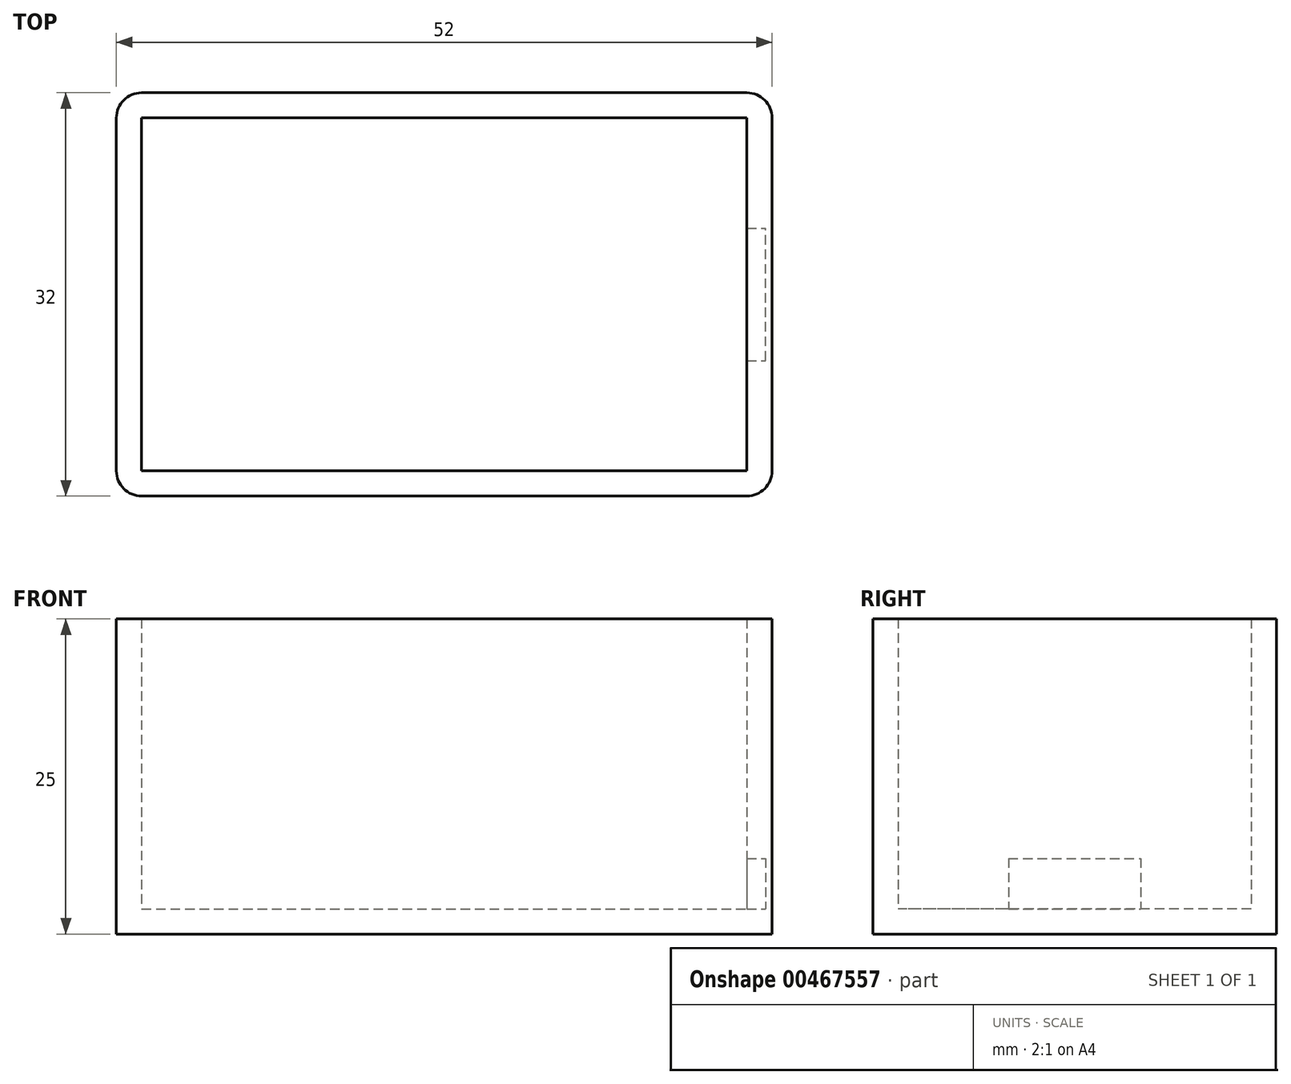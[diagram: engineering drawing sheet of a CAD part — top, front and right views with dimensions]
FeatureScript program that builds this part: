
annotation { "Feature Type Name" : "Feature", "Feature Type Description" : "" }
export const myFeature = defineFeature(function(context is Context, id is Id, definition is map)
    precondition{}
    {
        {
            var Q0;
            Q0=qCreatedBy(makeId("Top.planeOp"),FACE);
            var sketch = newSketch(context, id + "F0", { "sketchPlane" : qUnion([Q0])});
            skLineSegment(sketch, "E0.bottom", {"start": v(-24, 16) * mm, "end": v(24, 16) * mm});
            skLineSegment(sketch, "E0.top", {"start": v(-24, -16) * mm, "end": v(24, -16) * mm});
            skLineSegment(sketch, "E0.left", {"start": v(-26, 14) * mm, "end": v(-26, -14) * mm});
            skLineSegment(sketch, "E0.right", {"start": v(26, 14) * mm, "end": v(26, -14) * mm});
            skPoint(sketch, "E0.middle", {"position": v(0, 0) * mm});
            skPoint(sketch, "E1.visualSharp", {"position": v(-26, 16) * mm});
            skArc(sketch, "E1.filletArc", {"start": v(-24, 16) * mm, "mid": v(-25.41, 15.41) * mm, "end": v(-26, 14) * mm});
            skPoint(sketch, "E2.visualSharp", {"position": v(26, 16) * mm});
            skArc(sketch, "E2.filletArc", {"start": v(26, 14) * mm, "mid": v(25.41, 15.41) * mm, "end": v(24, 16) * mm});
            skPoint(sketch, "E3.visualSharp", {"position": v(-26, -16) * mm});
            skArc(sketch, "E3.filletArc", {"start": v(-26, -14) * mm, "mid": v(-25.41, -15.41) * mm, "end": v(-24, -16) * mm});
            skPoint(sketch, "E4.visualSharp", {"position": v(26, -16) * mm});
            skArc(sketch, "E4.filletArc", {"start": v(24, -16) * mm, "mid": v(25.41, -15.41) * mm, "end": v(26, -14) * mm});
            skSolve(sketch);
        }
        {
            var Q0;
            Q0=makeQuery(id+"F0.imprint","IMPRINT",FACE,{"disambiguationData":[TD([[makeQuery(id+"F0.imprint","IMPRINT",EDGE,{"derivedFrom":sQuery(id+"F0.wireOp",EDGE,"E0.bottom")}),-1.0]])]});
            extrude(context, id + "F1", {"entities" : qUnion([Q0]), "depth" : 25 * mm});
        }
        {
            var Q0;
            Q0=makeQuery(id+"F1.opExtrude","CAP_FACE",FACE,{"disambiguationData":[OSD([sQuery(id+"F0.wireOp",EDGE,"E0.bottom"),sQuery(id+"F0.wireOp",EDGE,"E0.top"),sQuery(id+"F0.wireOp",EDGE,"E0.left"),sQuery(id+"F0.wireOp",EDGE,"E0.right"),sQuery(id+"F0.wireOp",EDGE,"E1.filletArc"),sQuery(id+"F0.wireOp",EDGE,"E2.filletArc"),sQuery(id+"F0.wireOp",EDGE,"E3.filletArc"),sQuery(id+"F0.wireOp",EDGE,"E4.filletArc")])],"isStart":false});
            shell(context, id + "F2", {"entities" : qUnion([Q0]), "thickness" : 2 * mm});
        }
        {
            var Q0;
            Q0=qCreatedBy(makeId("Right.planeOp"),FACE);
            cPlane(context, id + "F3", {"entities" : qUnion([Q0]), "cplaneType" : CPlaneType.OFFSET, "offset" : 25.5 * mm, "width" : 150 * mm, "height" : 150 * mm});
        }
        {
            var Q0;
            Q0=qCreatedBy(id+"F3.planeOp",FACE);
            var sketch = newSketch(context, id + "F4", { "sketchPlane" : qUnion([Q0])});
            skPoint(sketch, "E5", {"position": v(0, 4) * mm});
            skLineSegment(sketch, "E6.bottom", {"start": v(-5.25, 6) * mm, "end": v(5.25, 6) * mm});
            skLineSegment(sketch, "E6.top", {"start": v(-5.25, 2) * mm, "end": v(5.25, 2) * mm});
            skLineSegment(sketch, "E6.left", {"start": v(-5.25, 6) * mm, "end": v(-5.25, 2) * mm});
            skLineSegment(sketch, "E6.right", {"start": v(5.25, 6) * mm, "end": v(5.25, 2) * mm});
            skSolve(sketch);
        }
        {
            var Q0;
            Q0=makeQuery(id+"F4.imprint","IMPRINT",FACE,{"disambiguationData":[TD([[makeQuery(id+"F4.imprint","IMPRINT",EDGE,{"derivedFrom":sQuery(id+"F4.wireOp",EDGE,"E6.bottom")}),-1.0]])]});
            extrude(context, id + "F5", {"entities" : qUnion([Q0]), "operationType" : NewBodyOperationType.REMOVE, "oppositeDirection" : true, "depth" : 3 * mm});
        }
    });
